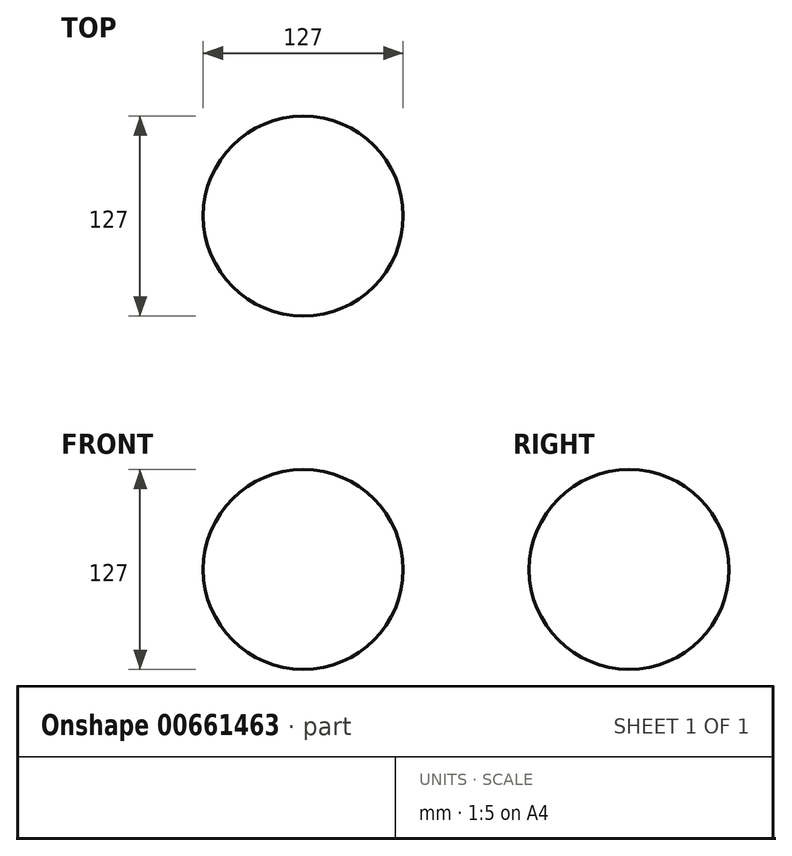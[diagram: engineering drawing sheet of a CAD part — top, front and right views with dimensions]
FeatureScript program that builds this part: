
annotation { "Feature Type Name" : "Feature", "Feature Type Description" : "" }
export const myFeature = defineFeature(function(context is Context, id is Id, definition is map)
    precondition{}
    {
        {
            var Q0;
            Q0=qCreatedBy(makeId("Front.planeOp"),FACE);
            var sketch = newSketch(context, id + "F0", { "sketchPlane" : qUnion([Q0])});
            skLineSegment(sketch, "E0", {"start": v(0, 63.5) * mm, "end": v(0, -63.5) * mm, "construction": true});
            skLineSegment(sketch, "E1", {"start": v(0, 63.5) * mm, "end": v(0, -63.5) * mm});
            skArc(sketch, "E2", {"start": v(0, -63.5) * mm, "mid": v(63.5, 0) * mm, "end": v(0, 63.5) * mm});
            skSolve(sketch);
        }
        {
            var Q0;
            Q0 = qSketchRegion(id + "F0", true);
            var Q1;
            Q1=sQuery(id+"F0.wireOp",EDGE,"E1");
            revolve(context, id + "F1", {"entities" : qUnion([Q0]), "axis" : qUnion([Q1]), "revolveType" : RevolveType.FULL});
        }
    });
